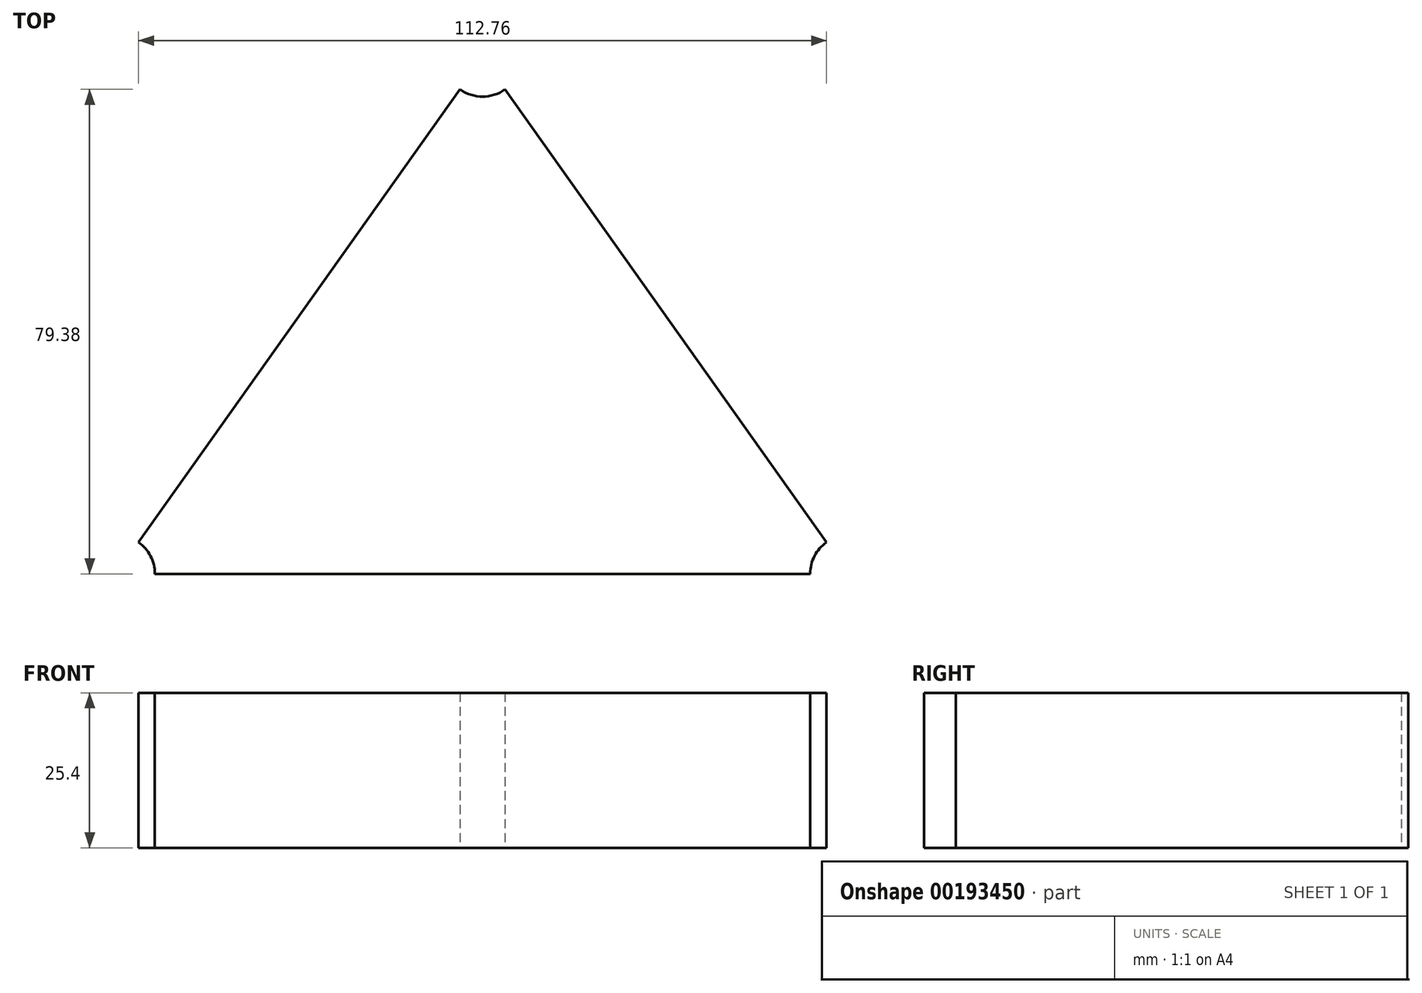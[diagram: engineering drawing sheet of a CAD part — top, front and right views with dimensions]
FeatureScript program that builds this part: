
annotation { "Feature Type Name" : "Feature", "Feature Type Description" : "" }
export const myFeature = defineFeature(function(context is Context, id is Id, definition is map)
    precondition{}
    {
        {
            var Q0;
            Q0=qCreatedBy(makeId("Top.planeOp"),FACE);
            var sketch = newSketch(context, id + "F0", { "sketchPlane" : qUnion([Q0])});
            skLineSegment(sketch, "E0", {"start": v(0, 0) * mm, "end": v(60.06, 84.56) * mm});
            skLineSegment(sketch, "E1", {"start": v(60.06, 84.56) * mm, "end": v(120.12, 0) * mm});
            skLineSegment(sketch, "E2", {"start": v(120.12, 0) * mm, "end": v(0, 0) * mm});
            skCircle(sketch, "E3", {"center": v(0, 0) * mm, "radius": 6.35 * mm});
            skCircle(sketch, "E4", {"center": v(60.06, 84.56) * mm, "radius": 6.35 * mm});
            skCircle(sketch, "E5", {"center": v(120.12, 0) * mm, "radius": 6.35 * mm});
            skSolve(sketch);
        }
        {
            var Q0;
            {var subQ0=sQuery(id+"F0.wireOp",EDGE,"E3");var subQ1=sQuery(id+"F0.wireOp",EDGE,"E0");var subQ2=makeQuery(id+"F0.imprint","INTERSECT",VERTEX,{"derivedFrom":[subQ1,subQ0]});Q0=makeQuery(id+"F0.imprint","IMPRINT",FACE,{"disambiguationData":[TD([[makeQuery(id+"F0.imprint","IMPRINT",EDGE,{"disambiguationData":[TD([[subQ2,-1.0]])],"derivedFrom":subQ1}),-1.0]])]});}
            extrude(context, id + "F1", {"entities" : qUnion([Q0]), "depth" : 25.4 * mm});
        }
    });
